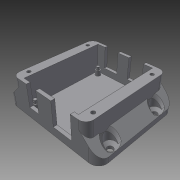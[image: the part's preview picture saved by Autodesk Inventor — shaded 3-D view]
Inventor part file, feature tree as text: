
AUTODESK INVENTOR PART (.ipt)
format: ipt  version: 2014 (Build 180170000, 170)  size: 446,976 bytes
history: native  units: mm
features: sketch x13, extrude x12, projected_geometry x11, fillet x2, hole x1, chamfer x1
ambient origin geometry x8: Origin, YZ Plane, XZ Plane, XY Plane, X Axis, Y Axis, Z Axis, Center Point
bodies: Solid1 (feature_tree)
feature tree (40):
  extrude  "Extrusion1"  Depth=50.0126mm
  extrude  "Extrusion2"  Depth=3.0mm
  extrude  "Extrusion3"  Depth=5.0mm
  extrude  "Extrusion4"  Depth=3.0mm
  extrude  "Extrusion5"  Depth=3.0mm
  extrude  "Extrusion6"  Depth=3.0mm TaperAngle=0.0deg
  extrude  "Extrusion7"  Depth=14.72mm
  extrude  "Extrusion8"  Depth=10.0mm
  extrude  "Extrusion9"  Depth=18.9mm TaperAngle=0.0deg
  extrude  "Extrusion10"  Depth=6.0mm
  extrude  "Extrusion11"  Depth=9.0mm
  hole  "Hole1"  [1 undecoded]
  chamfer  "Chamfer1"  Distance=3.2mm
  fillet  "Fillet2"  Radius=1.8mm
  fillet  "Fillet3"  Radius=6.2mm
  extrude  "Extrusion12"  Depth=8.0mm
  sketch  "Sketch1"  dims[d3=68.5038mm d4=50.0126mm]
  sketch  "Sketch2"  dims[d7=3.0mm d8=0.0mm d9=62.48mm]
  sketch  "Sketch3"  dims[d10=43.94mm d11=5.0mm]
  projected_geometry  "Projected Loop1"
  sketch  "Sketch4"  dims[d12=5.0mm d13=0.0mm d14=3.0mm]
  sketch  "Sketch5"  dims[d15=3.0mm d16=0.0mm d17=3.0mm]
  sketch  "Sketch6"  dims[d18=3.0mm d19=25.0mm d20=0.0mm]
  sketch  "Sketch7"  dims[d21=14.72mm d22=14.72mm]
  sketch  "Sketch8"  dims[d25=17.1mm d27=10.0mm]
  projected_geometry  "Projected Loop2"
  sketch  "Sketch9"  dims[d29=18.9mm d30=0.0mm d31=1.8mm d32=0.0mm]
  sketch  "Sketch10"  dims[d33=6.0mm d34=6.0mm]
  projected_geometry  "Projected Loop3"
  projected_geometry  "Projected Loop4"
  sketch  "Sketch11"  dims[d35=1.8mm d36=0.0mm d37=9.0mm]
  projected_geometry  "Projected Loop5"
  projected_geometry  "Projected Loop6"
  sketch  "Sketch12"  dims[d38=4.5mm d39=4.5mm]
  projected_geometry  "Projected Loop7"
  projected_geometry  "Projected Loop8"
  projected_geometry  "Projected Loop9"
  sketch  "Sketch13"  dims[d40=10.0mm d41=3.2mm d42=1.8mm d43=0.0mm d44=6.2mm d45=6.2mm d46=6.2mm d47=6.2mm d48=10.0mm d49=0.0mm d50=10.0mm d51=10.0mm d52=5.0mm d53=15.0mm d54=15.0mm d55=5.0mm d56=0.0mm d57=58.0mm d58=76.0mm d59=2.8mm d60=2.8mm d61=2.8mm d62=27.5mm d64=15.0mm d65=10.0mm d66=5.0mm d67=10.0mm d68=23.0mm d69=0.0mm d70=5.0mm d71=6.0mm d72=10.0mm d73=2.0mm d74=90.0deg d75=8.0mm d76=20.594885mm d77=2.0mm d78=2.0mm d79=45.0deg d80=6.0mm d81=8.0mm d82=0.8mm d83=0.0mm d84=0.0mm]
  projected_geometry  "Projected Loop10"
  projected_geometry  "Projected Loop11"
note: 1 required parameter value undecoded (feature->parameter linkage not recoverable at this tier; creation-order binding heuristic only, values carry confidence <= 0.55)
